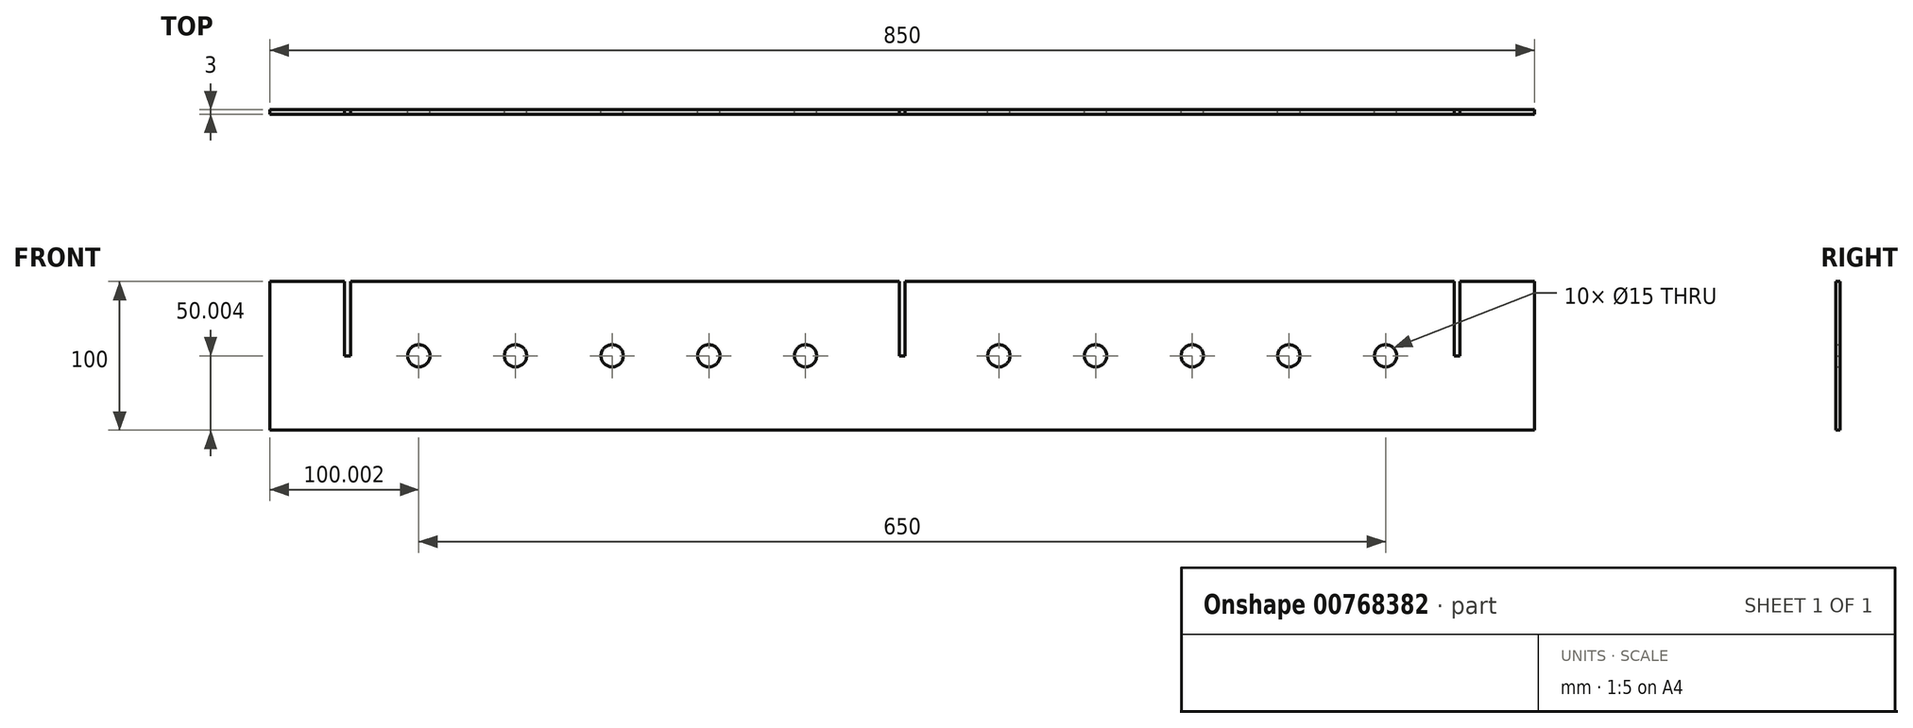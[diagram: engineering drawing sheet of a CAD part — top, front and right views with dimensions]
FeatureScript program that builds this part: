
annotation { "Feature Type Name" : "Feature", "Feature Type Description" : "" }
export const myFeature = defineFeature(function(context is Context, id is Id, definition is map)
    precondition{}
    {
        {
            var Q0;
            Q0=qCreatedBy(makeId("Front.planeOp"),FACE);
            var sketch = newSketch(context, id + "F0", { "sketchPlane" : qUnion([Q0])});
            skLineSegment(sketch, "E0.bottom", {"start": v(-459.78, -62.32) * mm, "end": v(390.22, -62.32) * mm});
            skLineSegment(sketch, "E0.top", {"start": v(-459.78, -162.32) * mm, "end": v(390.22, -162.32) * mm});
            skLineSegment(sketch, "E0.left", {"start": v(-459.78, -62.32) * mm, "end": v(-459.78, -162.32) * mm});
            skLineSegment(sketch, "E0.right", {"start": v(390.22, -62.32) * mm, "end": v(390.22, -162.32) * mm});
            skLineSegment(sketch, "E1.bottom", {"start": v(-409.78, -62.32) * mm, "end": v(-405.78, -62.32) * mm});
            skLineSegment(sketch, "E1.top", {"start": v(-409.78, -112.32) * mm, "end": v(-405.78, -112.32) * mm});
            skLineSegment(sketch, "E1.left", {"start": v(-409.78, -62.32) * mm, "end": v(-409.78, -112.32) * mm});
            skLineSegment(sketch, "E1.right", {"start": v(-405.78, -62.32) * mm, "end": v(-405.78, -112.32) * mm});
            skLineSegment(sketch, "E2.bottom", {"start": v(340.22, -62.32) * mm, "end": v(336.22, -62.32) * mm});
            skLineSegment(sketch, "E2.top", {"start": v(340.22, -112.32) * mm, "end": v(336.22, -112.32) * mm});
            skLineSegment(sketch, "E2.left", {"start": v(340.22, -62.32) * mm, "end": v(340.22, -112.32) * mm});
            skLineSegment(sketch, "E2.right", {"start": v(336.22, -62.32) * mm, "end": v(336.22, -112.32) * mm});
            skLineSegment(sketch, "E3.bottom", {"start": v(-36.78, -62.32) * mm, "end": v(-32.78, -62.32) * mm});
            skLineSegment(sketch, "E3.top", {"start": v(-36.78, -112.32) * mm, "end": v(-32.78, -112.32) * mm});
            skLineSegment(sketch, "E3.left", {"start": v(-36.78, -62.32) * mm, "end": v(-36.78, -112.32) * mm});
            skLineSegment(sketch, "E3.right", {"start": v(-32.78, -62.32) * mm, "end": v(-32.78, -112.32) * mm});
            skLineSegment(sketch, "E4", {"start": v(-459.78, -112.32) * mm, "end": v(390.22, -112.32) * mm, "construction": true});
            skCircle(sketch, "E5", {"center": v(-359.78, -112.32) * mm, "radius": 7.5 * mm});
            skCircle(sketch, "E6.1.0.0", {"center": v(-294.78, -112.32) * mm, "radius": 7.5 * mm});
            skCircle(sketch, "E6.2.0.0", {"center": v(-229.78, -112.32) * mm, "radius": 7.5 * mm});
            skCircle(sketch, "E6.3.0.0", {"center": v(-164.78, -112.32) * mm, "radius": 7.5 * mm});
            skCircle(sketch, "E6.4.0.0", {"center": v(-99.78, -112.32) * mm, "radius": 7.5 * mm});
            skCircle(sketch, "E6.6.0.0", {"center": v(30.22, -112.32) * mm, "radius": 7.5 * mm});
            skCircle(sketch, "E6.7.0.0", {"center": v(95.22, -112.32) * mm, "radius": 7.5 * mm});
            skCircle(sketch, "E6.8.0.0", {"center": v(160.22, -112.32) * mm, "radius": 7.5 * mm});
            skCircle(sketch, "E6.9.0.0", {"center": v(225.22, -112.32) * mm, "radius": 7.5 * mm});
            skCircle(sketch, "E6.10.0.0", {"center": v(290.22, -112.32) * mm, "radius": 7.5 * mm});
            skLineSegment(sketch, "E6.direction1", {"start": v(-359.78, -112.32) * mm, "end": v(-294.78, -112.32) * mm, "construction": true});
            skSolve(sketch);
        }
        {
            var Q0;
            Q0=makeQuery(id+"F0.imprint","IMPRINT",FACE,{"disambiguationData":[TD([[makeQuery(id+"F0.imprint","IMPRINT",EDGE,{"derivedFrom":sQuery(id+"F0.wireOp",EDGE,"E0.top")}),1.0]])]});
            extrude(context, id + "F1", {"entities" : qUnion([Q0]), "depth" : 3 * mm, "offsetDistance" : 25 * mm});
        }
    });
